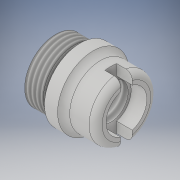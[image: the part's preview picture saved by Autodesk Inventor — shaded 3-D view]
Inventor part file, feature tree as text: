
AUTODESK INVENTOR PART (.ipt)
format: ipt  version: 2018.3 (Build 223284000, 284)  size: 200,704 bytes
history: native  units: in
note: dims shown in document units (in); Inventor stores cm internally (conversion verified against a paired STEP export)
features: sketch x2, revolve x1, hole x1, thread x1, plane x1, extrude x1
ambient origin geometry x8: Origin, YZ Plane, XZ Plane, XY Plane, X Axis, Y Axis, Z Axis, Center Point
bodies: Solid1 (feature_tree)
feature tree (7):
  revolve  "Revolution1"  [1 undecoded]
  hole  "Hole1"  [1 undecoded]
  thread  "Thread1"  [1 undecoded]
  plane  "Work Plane1"
  extrude  "Extrusion1"  Depth=0.045in
  sketch  "Sketch1"  dims[d0=0.279in d1=0.105in]
  sketch  "Sketch2"  dims[d2=0.1365in d3=0.05in d4=0.015in d5=0.118in d6=0.03in d7=0.177in d8=0.025in d9=60.0deg d10=0.0135in d11=60.0deg d12=90.0deg d22=1.0in d23=1.0in d15=0.134in d16=0.328in d17=0.19in d18=0.25in d19=0.5635in d20=0.467in d21=0.8108in d24=1.0in d25=0.0in d26=0.0in d27=0.156in d28=0.045in d29=0.06in d30=0.0in]
note: 3 required parameter values undecoded (feature->parameter linkage not recoverable at this tier; creation-order binding heuristic only, values carry confidence <= 0.55)